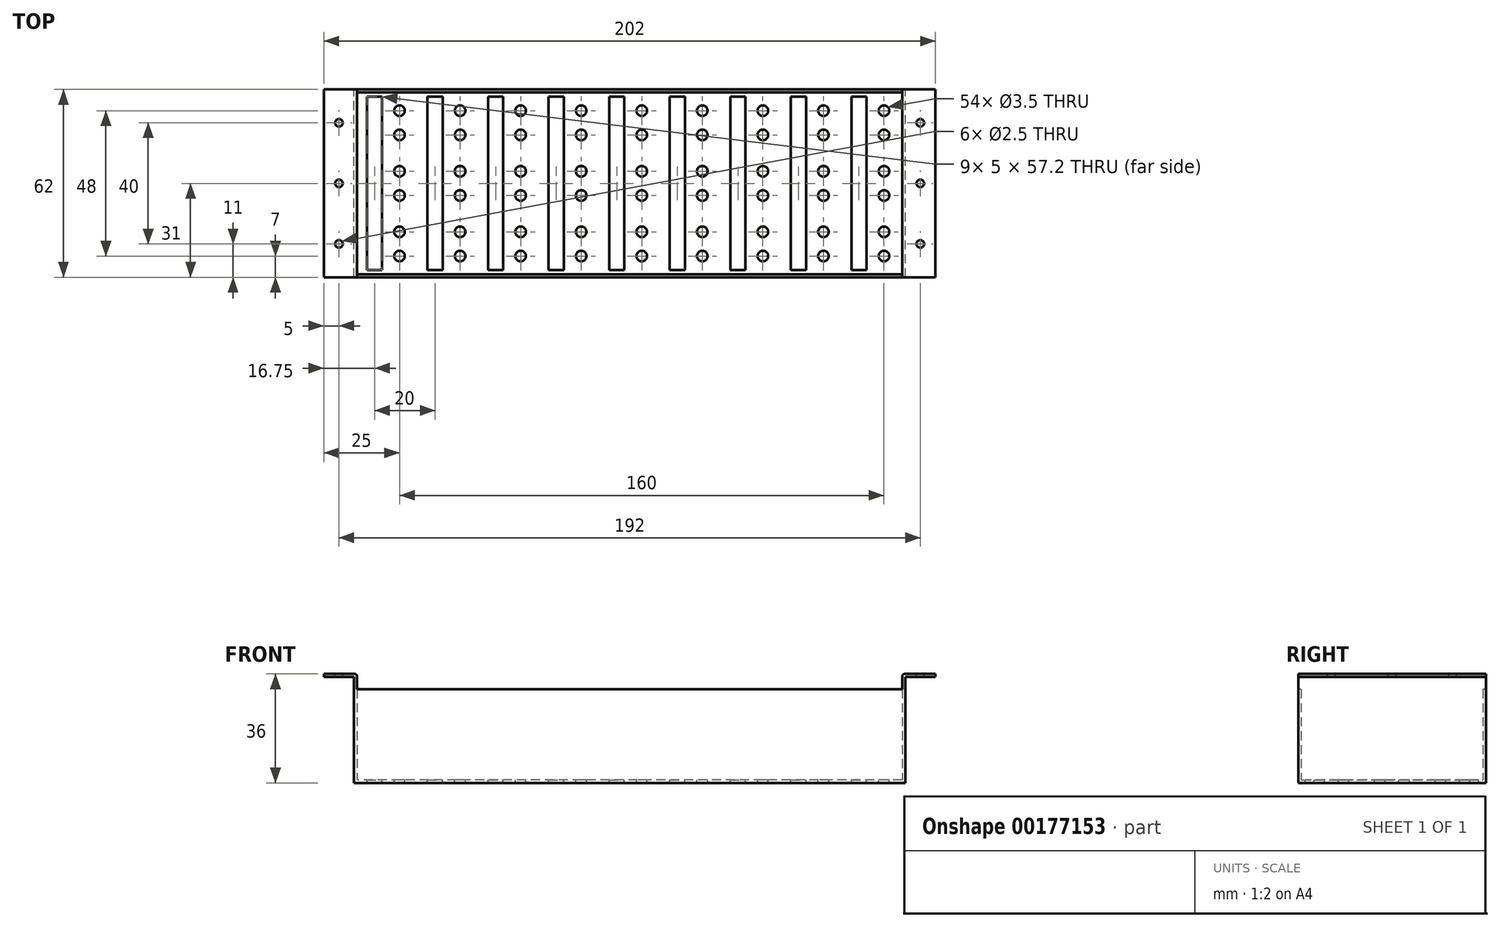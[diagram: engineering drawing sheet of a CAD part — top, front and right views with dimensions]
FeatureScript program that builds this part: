
annotation { "Feature Type Name" : "Feature", "Feature Type Description" : "" }
export const myFeature = defineFeature(function(context is Context, id is Id, definition is map)
    precondition{}
    {
        {
            var Q0;
            Q0=qCreatedBy(makeId("Top.planeOp"),FACE);
            var sketch = newSketch(context, id + "F0", { "sketchPlane" : qUnion([Q0])});
            skLineSegment(sketch, "E0.bottom", {"start": v(91, -31) * mm, "end": v(-91, -31) * mm});
            skLineSegment(sketch, "E0.top", {"start": v(91, 31) * mm, "end": v(-91, 31) * mm});
            skLineSegment(sketch, "E0.left", {"start": v(91, -31) * mm, "end": v(91, 31) * mm});
            skLineSegment(sketch, "E0.right", {"start": v(-91, -31) * mm, "end": v(-91, 31) * mm});
            skPoint(sketch, "E0.middle", {"position": v(0, 0) * mm});
            skSolve(sketch);
        }
        {
            var Q0;
            Q0 = qSketchRegion(id + "F0", true);
            extrude(context, id + "F1", {"entities" : qUnion([Q0]), "depth" : 36 * mm});
        }
        {
            var Q0;
            Q0=makeQuery(id+"F1.opExtrude","CAP_FACE",FACE,{"disambiguationData":[OSD([sQuery(id+"F0.wireOp",EDGE,"E0.bottom"),sQuery(id+"F0.wireOp",EDGE,"E0.top"),sQuery(id+"F0.wireOp",EDGE,"E0.left"),sQuery(id+"F0.wireOp",EDGE,"E0.right")])],"isStart":false});
            shell(context, id + "F2", {"entities" : qUnion([Q0]), "thickness" : 1 * mm});
        }
        {
            var Q0;
            Q0=makeQuery(id+"F1.opExtrude","CAP_FACE",FACE,{"disambiguationData":[OSD([sQuery(id+"F0.wireOp",EDGE,"E0.bottom"),sQuery(id+"F0.wireOp",EDGE,"E0.top"),sQuery(id+"F0.wireOp",EDGE,"E0.left"),sQuery(id+"F0.wireOp",EDGE,"E0.right")])],"isStart":false});
            var sketch = newSketch(context, id + "F3", { "sketchPlane" : qUnion([Q0])});
            skLineSegment(sketch, "E1.bottom", {"start": v(-91, 31) * mm, "end": v(-101, 31) * mm});
            skLineSegment(sketch, "E1.top", {"start": v(-91, -31) * mm, "end": v(-101, -31) * mm});
            skLineSegment(sketch, "E1.left", {"start": v(-91, 31) * mm, "end": v(-91, -31) * mm});
            skLineSegment(sketch, "E1.right", {"start": v(-101, 31) * mm, "end": v(-101, -31) * mm});
            skCircle(sketch, "E2", {"center": v(-96, 20) * mm, "radius": 1.25 * mm});
            skCircle(sketch, "E3", {"center": v(-96, 0) * mm, "radius": 1.25 * mm});
            skCircle(sketch, "E4", {"center": v(-96, -20) * mm, "radius": 1.25 * mm});
            skCircle(sketch, "E5.MirrorC", {"center": v(96, 20) * mm, "radius": 1.25 * mm});
            skCircle(sketch, "E6.MirrorC", {"center": v(96, 0) * mm, "radius": 1.25 * mm});
            skCircle(sketch, "E7.MirrorC", {"center": v(96, -20) * mm, "radius": 1.25 * mm});
            skLineSegment(sketch, "E8.MirrorCS", {"start": v(91, 31) * mm, "end": v(101, 31) * mm});
            skLineSegment(sketch, "E9.MirrorCS", {"start": v(91, -31) * mm, "end": v(101, -31) * mm});
            skLineSegment(sketch, "E10.MirrorCS", {"start": v(91, 31) * mm, "end": v(91, -31) * mm});
            skLineSegment(sketch, "E11.MirrorCS", {"start": v(101, 31) * mm, "end": v(101, -31) * mm});
            skSolve(sketch);
        }
        {
            var Q0;
            Q0 = qSketchRegion(id + "F3", true);
            extrude(context, id + "F4", {"entities" : qUnion([Q0]), "operationType" : NewBodyOperationType.ADD, "oppositeDirection" : true, "depth" : 1 * mm});
        }
        {
            var Q0;
            Q0=makeQuery(id+"F4.boolean.opBoolean","MERGE",FACE,{"derivedFrom":[makeQuery(id+"F1.opExtrude","SWEPT_FACE",FACE,{"disambiguationData":[OSD([sQuery(id+"F0.wireOp",EDGE,"E0.bottom")])]}),makeQuery(id+"F4.opExtrude","SWEPT_FACE",FACE,{"disambiguationData":[OSD([sQuery(id+"F3.wireOp",EDGE,"E1.top")])]}),makeQuery(id+"F4.opExtrude","SWEPT_FACE",FACE,{"disambiguationData":[OSD([sQuery(id+"F3.wireOp",EDGE,"E9.MirrorCS")])]})]});
            var sketch = newSketch(context, id + "F5", { "sketchPlane" : qUnion([Q0])});
            skLineSegment(sketch, "E12.bottom", {"start": v(-90, 39.58) * mm, "end": v(90, 39.58) * mm});
            skLineSegment(sketch, "E12.top", {"start": v(-90, 30.9) * mm, "end": v(90, 30.9) * mm});
            skLineSegment(sketch, "E12.left", {"start": v(-90, 39.58) * mm, "end": v(-90, 30.9) * mm});
            skLineSegment(sketch, "E12.right", {"start": v(90, 39.58) * mm, "end": v(90, 30.9) * mm});
            skSolve(sketch);
        }
        {
            var Q0;
            Q0 = qSketchRegion(id + "F5", true);
            extrude(context, id + "F6", {"entities" : qUnion([Q0]), "operationType" : NewBodyOperationType.REMOVE, "oppositeDirection" : true, "depth" : 70 * mm});
        }
        {
            var Q0;
            Q0=makeQuery(id+"F6.boolean.opBoolean","INTERSECT",EDGE,{"derivedFrom":[makeQuery(id+"F4.boolean.opBoolean","MERGE",FACE,{"derivedFrom":[makeQuery(id+"F1.opExtrude","CAP_FACE",FACE,{"disambiguationData":[OSD([sQuery(id+"F0.wireOp",EDGE,"E0.bottom"),sQuery(id+"F0.wireOp",EDGE,"E0.top"),sQuery(id+"F0.wireOp",EDGE,"E0.left"),sQuery(id+"F0.wireOp",EDGE,"E0.right")])],"isStart":false}),makeQuery(id+"F4.opExtrude","CAP_FACE",FACE,{"disambiguationData":[OSD([sQuery(id+"F3.wireOp",EDGE,"E1.bottom"),sQuery(id+"F3.wireOp",EDGE,"E1.top"),sQuery(id+"F3.wireOp",EDGE,"E1.left"),sQuery(id+"F3.wireOp",EDGE,"E1.right"),sQuery(id+"F3.wireOp",EDGE,"E2"),sQuery(id+"F3.wireOp",EDGE,"E3"),sQuery(id+"F3.wireOp",EDGE,"E4")])],"isStart":true}),makeQuery(id+"F4.opExtrude","CAP_FACE",FACE,{"disambiguationData":[OSD([sQuery(id+"F3.wireOp",EDGE,"E5.MirrorC"),sQuery(id+"F3.wireOp",EDGE,"E6.MirrorC"),sQuery(id+"F3.wireOp",EDGE,"E7.MirrorC"),sQuery(id+"F3.wireOp",EDGE,"E8.MirrorCS"),sQuery(id+"F3.wireOp",EDGE,"E9.MirrorCS"),sQuery(id+"F3.wireOp",EDGE,"E10.MirrorCS"),sQuery(id+"F3.wireOp",EDGE,"E11.MirrorCS")])],"isStart":true})]}),makeQuery(id+"F6.opExtrude","SWEPT_FACE",FACE,{"disambiguationData":[OSD([sQuery(id+"F5.wireOp",EDGE,"E12.left")])]})]});
            var Q1;
            Q1=makeQuery(id+"F4.opExtrude","CAP_EDGE",EDGE,{"disambiguationData":[OSD([sQuery(id+"F3.wireOp",EDGE,"E1.left")])],"isStart":false});
            var Q2;
            Q2=makeQuery(id+"F6.boolean.opBoolean","INTERSECT",EDGE,{"derivedFrom":[makeQuery(id+"F4.boolean.opBoolean","MERGE",FACE,{"derivedFrom":[makeQuery(id+"F1.opExtrude","CAP_FACE",FACE,{"disambiguationData":[OSD([sQuery(id+"F0.wireOp",EDGE,"E0.bottom"),sQuery(id+"F0.wireOp",EDGE,"E0.top"),sQuery(id+"F0.wireOp",EDGE,"E0.left"),sQuery(id+"F0.wireOp",EDGE,"E0.right")])],"isStart":false}),makeQuery(id+"F4.opExtrude","CAP_FACE",FACE,{"disambiguationData":[OSD([sQuery(id+"F3.wireOp",EDGE,"E1.bottom"),sQuery(id+"F3.wireOp",EDGE,"E1.top"),sQuery(id+"F3.wireOp",EDGE,"E1.left"),sQuery(id+"F3.wireOp",EDGE,"E1.right"),sQuery(id+"F3.wireOp",EDGE,"E2"),sQuery(id+"F3.wireOp",EDGE,"E3"),sQuery(id+"F3.wireOp",EDGE,"E4")])],"isStart":true}),makeQuery(id+"F4.opExtrude","CAP_FACE",FACE,{"disambiguationData":[OSD([sQuery(id+"F3.wireOp",EDGE,"E5.MirrorC"),sQuery(id+"F3.wireOp",EDGE,"E6.MirrorC"),sQuery(id+"F3.wireOp",EDGE,"E7.MirrorC"),sQuery(id+"F3.wireOp",EDGE,"E8.MirrorCS"),sQuery(id+"F3.wireOp",EDGE,"E9.MirrorCS"),sQuery(id+"F3.wireOp",EDGE,"E10.MirrorCS"),sQuery(id+"F3.wireOp",EDGE,"E11.MirrorCS")])],"isStart":true})]}),makeQuery(id+"F6.opExtrude","SWEPT_FACE",FACE,{"disambiguationData":[OSD([sQuery(id+"F5.wireOp",EDGE,"E12.right")])]})]});
            var Q3;
            Q3=makeQuery(id+"F4.opExtrude","CAP_EDGE",EDGE,{"disambiguationData":[OSD([sQuery(id+"F3.wireOp",EDGE,"E10.MirrorCS")])],"isStart":false});
            fillet(context, id + "F7", {"entities" : qUnion([Q0, Q1, Q2, Q3]), "radius" : 1 * mm, "tangentPropagation" : true, "allowEdgeOverflow" : false});
        }
        {
            var Q0;
            Q0=makeQuery(id+"F2.opShell","OFFSET_FACE",FACE,{"disambiguationData":[OSD([sQuery(id+"F0.wireOp",EDGE,"E0.bottom"),sQuery(id+"F0.wireOp",EDGE,"E0.top"),sQuery(id+"F0.wireOp",EDGE,"E0.left"),sQuery(id+"F0.wireOp",EDGE,"E0.right")])]});
            var sketch = newSketch(context, id + "F8", { "sketchPlane" : qUnion([Q0])});
            skCircle(sketch, "E13", {"center": v(-76, 24) * mm, "radius": 1.75 * mm});
            skCircle(sketch, "E14", {"center": v(-76, 16) * mm, "radius": 1.75 * mm});
            skCircle(sketch, "E15.0.1.0", {"center": v(-76, 4) * mm, "radius": 1.75 * mm});
            skCircle(sketch, "E15.0.1.1", {"center": v(-76, -4) * mm, "radius": 1.75 * mm});
            skCircle(sketch, "E15.0.2.0", {"center": v(-76, -16) * mm, "radius": 1.75 * mm});
            skCircle(sketch, "E15.0.2.1", {"center": v(-76, -24) * mm, "radius": 1.75 * mm});
            skCircle(sketch, "E15.1.0.0", {"center": v(-56, 24) * mm, "radius": 1.75 * mm});
            skCircle(sketch, "E15.1.0.1", {"center": v(-56, 16) * mm, "radius": 1.75 * mm});
            skCircle(sketch, "E15.1.1.0", {"center": v(-56, 4) * mm, "radius": 1.75 * mm});
            skCircle(sketch, "E15.1.1.1", {"center": v(-56, -4) * mm, "radius": 1.75 * mm});
            skCircle(sketch, "E15.1.2.0", {"center": v(-56, -16) * mm, "radius": 1.75 * mm});
            skCircle(sketch, "E15.1.2.1", {"center": v(-56, -24) * mm, "radius": 1.75 * mm});
            skCircle(sketch, "E15.2.0.0", {"center": v(-36, 24) * mm, "radius": 1.75 * mm});
            skCircle(sketch, "E15.2.0.1", {"center": v(-36, 16) * mm, "radius": 1.75 * mm});
            skCircle(sketch, "E15.2.1.0", {"center": v(-36, 4) * mm, "radius": 1.75 * mm});
            skCircle(sketch, "E15.2.1.1", {"center": v(-36, -4) * mm, "radius": 1.75 * mm});
            skCircle(sketch, "E15.2.2.0", {"center": v(-36, -16) * mm, "radius": 1.75 * mm});
            skCircle(sketch, "E15.2.2.1", {"center": v(-36, -24) * mm, "radius": 1.75 * mm});
            skCircle(sketch, "E15.3.0.0", {"center": v(-16, 24) * mm, "radius": 1.75 * mm});
            skCircle(sketch, "E15.3.0.1", {"center": v(-16, 16) * mm, "radius": 1.75 * mm});
            skCircle(sketch, "E15.3.1.0", {"center": v(-16, 4) * mm, "radius": 1.75 * mm});
            skCircle(sketch, "E15.3.1.1", {"center": v(-16, -4) * mm, "radius": 1.75 * mm});
            skCircle(sketch, "E15.3.2.0", {"center": v(-16, -16) * mm, "radius": 1.75 * mm});
            skCircle(sketch, "E15.3.2.1", {"center": v(-16, -24) * mm, "radius": 1.75 * mm});
            skCircle(sketch, "E15.4.0.0", {"center": v(4, 24) * mm, "radius": 1.75 * mm});
            skCircle(sketch, "E15.4.0.1", {"center": v(4, 16) * mm, "radius": 1.75 * mm});
            skCircle(sketch, "E15.4.1.0", {"center": v(4, 4) * mm, "radius": 1.75 * mm});
            skCircle(sketch, "E15.4.1.1", {"center": v(4, -4) * mm, "radius": 1.75 * mm});
            skCircle(sketch, "E15.4.2.0", {"center": v(4, -16) * mm, "radius": 1.75 * mm});
            skCircle(sketch, "E15.4.2.1", {"center": v(4, -24) * mm, "radius": 1.75 * mm});
            skCircle(sketch, "E15.5.0.0", {"center": v(24, 24) * mm, "radius": 1.75 * mm});
            skCircle(sketch, "E15.5.0.1", {"center": v(24, 16) * mm, "radius": 1.75 * mm});
            skCircle(sketch, "E15.5.1.0", {"center": v(24, 4) * mm, "radius": 1.75 * mm});
            skCircle(sketch, "E15.5.1.1", {"center": v(24, -4) * mm, "radius": 1.75 * mm});
            skCircle(sketch, "E15.5.2.0", {"center": v(24, -16) * mm, "radius": 1.75 * mm});
            skCircle(sketch, "E15.5.2.1", {"center": v(24, -24) * mm, "radius": 1.75 * mm});
            skCircle(sketch, "E15.6.0.0", {"center": v(44, 24) * mm, "radius": 1.75 * mm});
            skCircle(sketch, "E15.6.0.1", {"center": v(44, 16) * mm, "radius": 1.75 * mm});
            skCircle(sketch, "E15.6.1.0", {"center": v(44, 4) * mm, "radius": 1.75 * mm});
            skCircle(sketch, "E15.6.1.1", {"center": v(44, -4) * mm, "radius": 1.75 * mm});
            skCircle(sketch, "E15.6.2.0", {"center": v(44, -16) * mm, "radius": 1.75 * mm});
            skCircle(sketch, "E15.6.2.1", {"center": v(44, -24) * mm, "radius": 1.75 * mm});
            skCircle(sketch, "E15.7.0.0", {"center": v(64, 24) * mm, "radius": 1.75 * mm});
            skCircle(sketch, "E15.7.0.1", {"center": v(64, 16) * mm, "radius": 1.75 * mm});
            skCircle(sketch, "E15.7.1.0", {"center": v(64, 4) * mm, "radius": 1.75 * mm});
            skCircle(sketch, "E15.7.1.1", {"center": v(64, -4) * mm, "radius": 1.75 * mm});
            skCircle(sketch, "E15.7.2.0", {"center": v(64, -16) * mm, "radius": 1.75 * mm});
            skCircle(sketch, "E15.7.2.1", {"center": v(64, -24) * mm, "radius": 1.75 * mm});
            skCircle(sketch, "E15.8.0.0", {"center": v(84, 24) * mm, "radius": 1.75 * mm});
            skCircle(sketch, "E15.8.0.1", {"center": v(84, 16) * mm, "radius": 1.75 * mm});
            skCircle(sketch, "E15.8.1.0", {"center": v(84, 4) * mm, "radius": 1.75 * mm});
            skCircle(sketch, "E15.8.1.1", {"center": v(84, -4) * mm, "radius": 1.75 * mm});
            skCircle(sketch, "E15.8.2.0", {"center": v(84, -16) * mm, "radius": 1.75 * mm});
            skCircle(sketch, "E15.8.2.1", {"center": v(84, -24) * mm, "radius": 1.75 * mm});
            skLineSegment(sketch, "E15.direction1", {"start": v(-76, 24) * mm, "end": v(-56, 24) * mm, "construction": true});
            skLineSegment(sketch, "E15.direction2", {"start": v(-76, 24) * mm, "end": v(-76, 4) * mm, "construction": true});
            skLineSegment(sketch, "E16.bottom", {"start": v(-86.75, 28.6) * mm, "end": v(-81.75, 28.6) * mm});
            skLineSegment(sketch, "E16.top", {"start": v(-86.75, -28.6) * mm, "end": v(-81.75, -28.6) * mm});
            skLineSegment(sketch, "E16.left", {"start": v(-86.75, 28.6) * mm, "end": v(-86.75, -28.6) * mm});
            skLineSegment(sketch, "E16.right", {"start": v(-81.75, 28.6) * mm, "end": v(-81.75, -28.6) * mm});
            skLineSegment(sketch, "E17.1.0.0", {"start": v(-66.75, 28.6) * mm, "end": v(-66.75, -28.6) * mm});
            skLineSegment(sketch, "E17.1.0.1", {"start": v(-66.75, -28.6) * mm, "end": v(-61.75, -28.6) * mm});
            skLineSegment(sketch, "E17.1.0.2", {"start": v(-66.75, 28.6) * mm, "end": v(-61.75, 28.6) * mm});
            skLineSegment(sketch, "E17.1.0.3", {"start": v(-61.75, 28.6) * mm, "end": v(-61.75, -28.6) * mm});
            skLineSegment(sketch, "E17.2.0.0", {"start": v(-46.75, 28.6) * mm, "end": v(-46.75, -28.6) * mm});
            skLineSegment(sketch, "E17.2.0.1", {"start": v(-46.75, -28.6) * mm, "end": v(-41.75, -28.6) * mm});
            skLineSegment(sketch, "E17.2.0.2", {"start": v(-46.75, 28.6) * mm, "end": v(-41.75, 28.6) * mm});
            skLineSegment(sketch, "E17.2.0.3", {"start": v(-41.75, 28.6) * mm, "end": v(-41.75, -28.6) * mm});
            skLineSegment(sketch, "E17.3.0.0", {"start": v(-26.75, 28.6) * mm, "end": v(-26.75, -28.6) * mm});
            skLineSegment(sketch, "E17.3.0.1", {"start": v(-26.75, -28.6) * mm, "end": v(-21.75, -28.6) * mm});
            skLineSegment(sketch, "E17.3.0.2", {"start": v(-26.75, 28.6) * mm, "end": v(-21.75, 28.6) * mm});
            skLineSegment(sketch, "E17.3.0.3", {"start": v(-21.75, 28.6) * mm, "end": v(-21.75, -28.6) * mm});
            skLineSegment(sketch, "E17.4.0.0", {"start": v(-6.75, 28.6) * mm, "end": v(-6.75, -28.6) * mm});
            skLineSegment(sketch, "E17.4.0.1", {"start": v(-6.75, -28.6) * mm, "end": v(-1.75, -28.6) * mm});
            skLineSegment(sketch, "E17.4.0.2", {"start": v(-6.75, 28.6) * mm, "end": v(-1.75, 28.6) * mm});
            skLineSegment(sketch, "E17.4.0.3", {"start": v(-1.75, 28.6) * mm, "end": v(-1.75, -28.6) * mm});
            skLineSegment(sketch, "E17.5.0.0", {"start": v(13.25, 28.6) * mm, "end": v(13.25, -28.6) * mm});
            skLineSegment(sketch, "E17.5.0.1", {"start": v(13.25, -28.6) * mm, "end": v(18.25, -28.6) * mm});
            skLineSegment(sketch, "E17.5.0.2", {"start": v(13.25, 28.6) * mm, "end": v(18.25, 28.6) * mm});
            skLineSegment(sketch, "E17.5.0.3", {"start": v(18.25, 28.6) * mm, "end": v(18.25, -28.6) * mm});
            skLineSegment(sketch, "E17.6.0.0", {"start": v(33.25, 28.6) * mm, "end": v(33.25, -28.6) * mm});
            skLineSegment(sketch, "E17.6.0.1", {"start": v(33.25, -28.6) * mm, "end": v(38.25, -28.6) * mm});
            skLineSegment(sketch, "E17.6.0.2", {"start": v(33.25, 28.6) * mm, "end": v(38.25, 28.6) * mm});
            skLineSegment(sketch, "E17.6.0.3", {"start": v(38.25, 28.6) * mm, "end": v(38.25, -28.6) * mm});
            skLineSegment(sketch, "E17.7.0.0", {"start": v(53.25, 28.6) * mm, "end": v(53.25, -28.6) * mm});
            skLineSegment(sketch, "E17.7.0.1", {"start": v(53.25, -28.6) * mm, "end": v(58.25, -28.6) * mm});
            skLineSegment(sketch, "E17.7.0.2", {"start": v(53.25, 28.6) * mm, "end": v(58.25, 28.6) * mm});
            skLineSegment(sketch, "E17.7.0.3", {"start": v(58.25, 28.6) * mm, "end": v(58.25, -28.6) * mm});
            skLineSegment(sketch, "E17.8.0.0", {"start": v(73.25, 28.6) * mm, "end": v(73.25, -28.6) * mm});
            skLineSegment(sketch, "E17.8.0.1", {"start": v(73.25, -28.6) * mm, "end": v(78.25, -28.6) * mm});
            skLineSegment(sketch, "E17.8.0.2", {"start": v(73.25, 28.6) * mm, "end": v(78.25, 28.6) * mm});
            skLineSegment(sketch, "E17.8.0.3", {"start": v(78.25, 28.6) * mm, "end": v(78.25, -28.6) * mm});
            skLineSegment(sketch, "E17.direction1", {"start": v(-86.75, -28.6) * mm, "end": v(-66.75, -28.6) * mm, "construction": true});
            skSolve(sketch);
        }
        {
            var Q0;
            Q0 = qSketchRegion(id + "F8", true);
            extrude(context, id + "F9", {"entities" : qUnion([Q0]), "operationType" : NewBodyOperationType.REMOVE, "oppositeDirection" : true, "depth" : 25 * mm});
        }
    });
